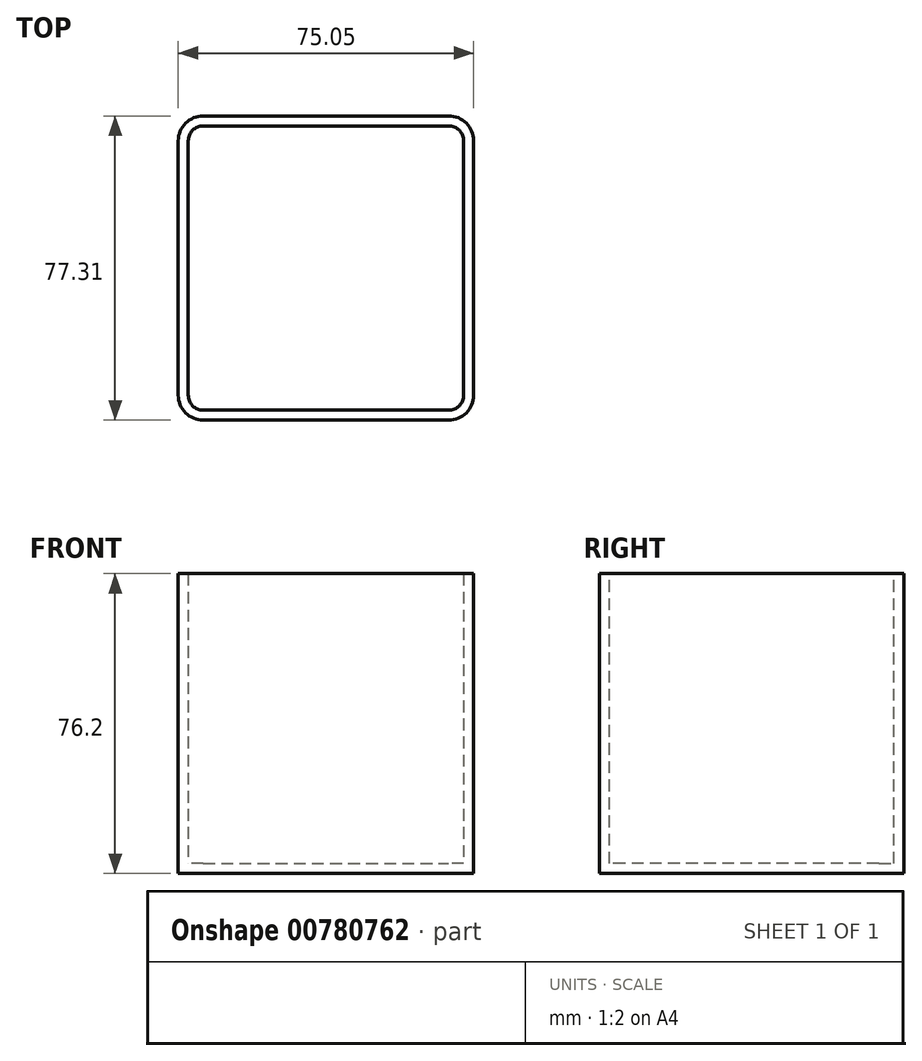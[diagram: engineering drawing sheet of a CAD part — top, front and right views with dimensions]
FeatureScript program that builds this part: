
annotation { "Feature Type Name" : "Feature", "Feature Type Description" : "" }
export const myFeature = defineFeature(function(context is Context, id is Id, definition is map)
    precondition{}
    {
        {
            var Q0;
            Q0=qCreatedBy(makeId("Top.planeOp"),FACE);
            var sketch = newSketch(context, id + "F0", { "sketchPlane" : qUnion([Q0])});
            skLineSegment(sketch, "E0.bottom", {"start": v(-36.51, 37.5) * mm, "end": v(38.54, 37.5) * mm});
            skLineSegment(sketch, "E0.top", {"start": v(-36.51, -39.82) * mm, "end": v(38.54, -39.82) * mm});
            skLineSegment(sketch, "E0.left", {"start": v(-36.51, 37.5) * mm, "end": v(-36.51, -39.82) * mm});
            skLineSegment(sketch, "E0.right", {"start": v(38.54, 37.5) * mm, "end": v(38.54, -39.82) * mm});
            skSolve(sketch);
        }
        {
            var Q0;
            Q0 = qSketchRegion(id + "F0", true);
            extrude(context, id + "F1", {"entities" : qUnion([Q0]), "depth" : 76.2 * mm, "offsetDistance" : 25.4 * mm});
        }
        {
            var Q0;
            Q0=makeQuery(id+"F1.opExtrude","SWEPT_EDGE",EDGE,{"disambiguationData":[OSD([sQuery(id+"F0.wireOp",EDGE,"E0.top"),sQuery(id+"F0.wireOp",EDGE,"E0.left")])]});
            var Q1;
            Q1=makeQuery(id+"F1.opExtrude","SWEPT_EDGE",EDGE,{"disambiguationData":[OSD([sQuery(id+"F0.wireOp",EDGE,"E0.bottom"),sQuery(id+"F0.wireOp",EDGE,"E0.left")])]});
            var Q2;
            Q2=makeQuery(id+"F1.opExtrude","SWEPT_EDGE",EDGE,{"disambiguationData":[OSD([sQuery(id+"F0.wireOp",EDGE,"E0.bottom"),sQuery(id+"F0.wireOp",EDGE,"E0.right")])]});
            var Q3;
            Q3=makeQuery(id+"F1.opExtrude","SWEPT_EDGE",EDGE,{"disambiguationData":[OSD([sQuery(id+"F0.wireOp",EDGE,"E0.top"),sQuery(id+"F0.wireOp",EDGE,"E0.right")])]});
            fillet(context, id + "F2", {"entities" : qUnion([Q0, Q1, Q2, Q3]), "radius" : 6.35 * mm, "tangentPropagation" : true, "allowEdgeOverflow" : false});
        }
        {
            var Q0;
            Q0=makeQuery(id+"F1.opExtrude","CAP_FACE",FACE,{"disambiguationData":[OSD([sQuery(id+"F0.wireOp",EDGE,"E0.bottom"),sQuery(id+"F0.wireOp",EDGE,"E0.top"),sQuery(id+"F0.wireOp",EDGE,"E0.left"),sQuery(id+"F0.wireOp",EDGE,"E0.right")])],"isStart":false});
            shell(context, id + "F3", {"entities" : qUnion([Q0]), "thickness" : 2.54 * mm});
        }
    });
